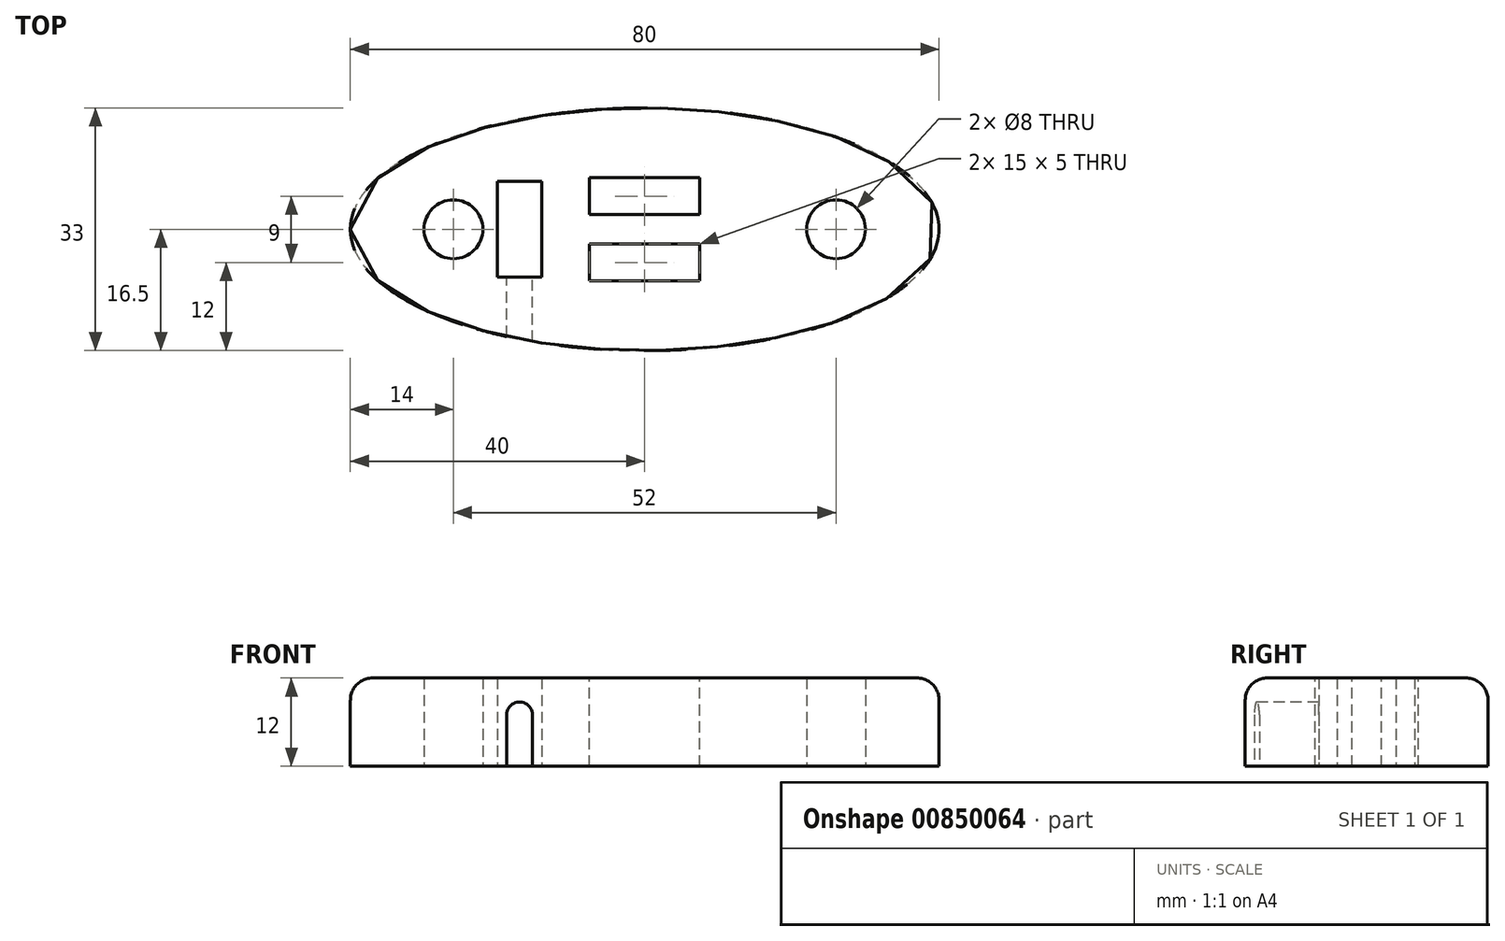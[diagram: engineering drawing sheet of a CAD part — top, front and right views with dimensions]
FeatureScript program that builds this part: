
annotation { "Feature Type Name" : "Feature", "Feature Type Description" : "" }
export const myFeature = defineFeature(function(context is Context, id is Id, definition is map)
    precondition{}
    {
        {
            var Q0;
            Q0=qCreatedBy(makeId("Top.planeOp"),FACE);
            var sketch = newSketch(context, id + "F0", { "sketchPlane" : qUnion([Q0])});
            skEllipse(sketch, "E0", {"center": v(0, 0) * mm, "majorRadius": 40 * mm, "minorRadius": 16.5 * mm, "majorAxis": v(-1, 0)});
            skSolve(sketch);
        }
        {
            var Q0;
            Q0 = qSketchRegion(id + "F0", true);
            extrude(context, id + "F1", {"entities" : qUnion([Q0]), "depth" : 12 * mm, "offsetDistance" : 25 * mm});
        }
        {
            var Q0;
            Q0=makeQuery(id+"F1.opExtrude","CAP_EDGE",EDGE,{"disambiguationData":[OSD([sQuery(id+"F0.wireOp",EDGE,"E0")])],"isStart":false});
            fillet(context, id + "F2", {"entities" : qUnion([Q0]), "radius" : 3 * mm, "tangentPropagation" : true, "allowEdgeOverflow" : false});
        }
        {
            var Q0;
            Q0=makeQuery(id+"F1.opExtrude","CAP_FACE",FACE,{"disambiguationData":[OSD([sQuery(id+"F0.wireOp",EDGE,"E0")])],"isStart":false});
            var sketch = newSketch(context, id + "F3", { "sketchPlane" : qUnion([Q0])});
            skLineSegment(sketch, "E1", {"start": v(0, 0) * mm, "end": v(0, -2) * mm});
            skLineSegment(sketch, "E2", {"start": v(0, -2) * mm, "end": v(-7.5, -2) * mm});
            skLineSegment(sketch, "E3.bottom", {"start": v(-7.5, -2) * mm, "end": v(7.5, -2) * mm});
            skLineSegment(sketch, "E3.top", {"start": v(-7.5, -7) * mm, "end": v(7.5, -7) * mm});
            skLineSegment(sketch, "E3.left", {"start": v(-7.5, -2) * mm, "end": v(-7.5, -7) * mm});
            skLineSegment(sketch, "E3.right", {"start": v(7.5, -2) * mm, "end": v(7.5, -7) * mm});
            skLineSegment(sketch, "E4", {"start": v(0, 0) * mm, "end": v(0, 2) * mm});
            skPoint(sketch, "E5.oppositeSnap0", {"position": v(7.5, -4.5) * mm});
            skLineSegment(sketch, "E5.bottom", {"start": v(-7.5, 2) * mm, "end": v(7.5, 2) * mm});
            skLineSegment(sketch, "E5.top", {"start": v(-7.5, 7) * mm, "end": v(7.5, 7) * mm});
            skLineSegment(sketch, "E5.left", {"start": v(-7.5, 2) * mm, "end": v(-7.5, 7) * mm});
            skLineSegment(sketch, "E5.right", {"start": v(7.5, 2) * mm, "end": v(7.5, 7) * mm});
            skSolve(sketch);
        }
        {
            var Q0;
            Q0=makeQuery(id+"F3.imprint","IMPRINT",FACE,{"disambiguationData":[TD([[makeQuery(id+"F3.imprint","IMPRINT",EDGE,{"derivedFrom":sQuery(id+"F3.wireOp",EDGE,"E3.top")}),1.0]])]});
            var Q1;
            Q1=makeQuery(id+"F3.imprint","IMPRINT",FACE,{"disambiguationData":[TD([[makeQuery(id+"F3.imprint","IMPRINT",EDGE,{"derivedFrom":sQuery(id+"F3.wireOp",EDGE,"E5.top")}),-1.0]])]});
            extrude(context, id + "F4", {"entities" : qUnion([Q0, Q1]), "operationType" : NewBodyOperationType.REMOVE, "endBound" : BoundingType.THROUGH_ALL, "oppositeDirection" : true, "depth" : 18.8 * mm, "offsetDistance" : 25 * mm});
        }
        {
            var Q0;
            Q0=makeQuery(id+"F1.opExtrude","CAP_FACE",FACE,{"disambiguationData":[OSD([sQuery(id+"F0.wireOp",EDGE,"E0")])],"isStart":true});
            var sketch = newSketch(context, id + "F5", { "sketchPlane" : qUnion([Q0])});
            skLineSegment(sketch, "E6", {"start": v(40, 0) * mm, "end": v(26, 0) * mm});
            skLineSegment(sketch, "E7", {"start": v(-40, 0) * mm, "end": v(-26, 0) * mm});
            skCircle(sketch, "E8", {"center": v(26, 0) * mm, "radius": 4 * mm});
            skCircle(sketch, "E9", {"center": v(-26, 0) * mm, "radius": 4 * mm});
            skLineSegment(sketch, "E10", {"start": v(-26, 0) * mm, "end": v(-20, 0) * mm});
            skLineSegment(sketch, "E11", {"start": v(-20, 0) * mm, "end": v(-20, -6.5) * mm});
            skLineSegment(sketch, "E12.bottom", {"start": v(-20, -6.5) * mm, "end": v(-14, -6.5) * mm});
            skLineSegment(sketch, "E12.top", {"start": v(-20, 6.5) * mm, "end": v(-14, 6.5) * mm});
            skLineSegment(sketch, "E12.left", {"start": v(-20, -6.5) * mm, "end": v(-20, 6.5) * mm});
            skLineSegment(sketch, "E12.right", {"start": v(-14, -6.5) * mm, "end": v(-14, 6.5) * mm});
            skSolve(sketch);
        }
        {
            var Q0;
            Q0 = qSketchRegion(id + "F5", true);
            extrude(context, id + "F6", {"entities" : qUnion([Q0]), "operationType" : NewBodyOperationType.REMOVE, "oppositeDirection" : true, "depth" : 53.1 * mm, "offsetDistance" : 25 * mm});
        }
        {
            var Q0;
            Q0=makeQuery(id+"F6.boolean.opBoolean","COPY",FACE,{"derivedFrom":makeQuery(id+"F6.opExtrude","SWEPT_FACE",FACE,{"disambiguationData":[OSD([sQuery(id+"F5.wireOp",EDGE,"E12.top")])]})});
            var sketch = newSketch(context, id + "F7", { "sketchPlane" : qUnion([Q0])});
            skLineSegment(sketch, "E13", {"start": v(17, 0) * mm, "end": v(17, 7) * mm});
            skLineSegment(sketch, "E14", {"start": v(17, 0) * mm, "end": v(15, 0) * mm});
            skCircle(sketch, "E15", {"center": v(17, 7) * mm, "radius": 1.75 * mm});
            skLineSegment(sketch, "E16", {"start": v(15.25, 7) * mm, "end": v(15.25, 0) * mm});
            skLineSegment(sketch, "E17", {"start": v(18.75, 7) * mm, "end": v(18.75, 0) * mm});
            skSolve(sketch);
        }
        {
            var Q0;
            {var subQ0=sQuery(id+"F7.wireOp",EDGE,"qlNYMipe-BtAs-6Y4S-IRvH-gPQyJQVTGbDt");var subQ1=sQuery(id+"F7.wireOp",EDGE,"E13");var subQ2=makeQuery(id+"F7.imprint","INTERSECT",VERTEX,{"derivedFrom":[subQ1,subQ0]});Q0=makeQuery(id+"F7.imprint","IMPRINT",FACE,{"disambiguationData":[TD([[makeQuery(id+"F7.imprint","IMPRINT",EDGE,{"disambiguationData":[TD([[subQ2,1.0]])],"derivedFrom":subQ1}),-1.0]])]});}
            var Q1;
            {var subQ0=sQuery(id+"F7.wireOp",EDGE,"qlNYMipe-BtAs-6Y4S-IRvH-gPQyJQVTGbDt");var subQ1=sQuery(id+"F7.wireOp",EDGE,"E13");var subQ2=makeQuery(id+"F7.imprint","INTERSECT",VERTEX,{"derivedFrom":[subQ1,subQ0]});Q1=makeQuery(id+"F7.imprint","IMPRINT",FACE,{"disambiguationData":[TD([[makeQuery(id+"F7.imprint","IMPRINT",EDGE,{"disambiguationData":[TD([[subQ2,1.0]])],"derivedFrom":subQ1}),1.0]])]});}
            var Q2;
            {var subQ0=sQuery(id+"F7.wireOp",EDGE,"qlNYMipe-BtAs-6Y4S-IRvH-gPQyJQVTGbDt");var subQ4=makeQuery(id+"F7.imprint","INTERSECT",VERTEX,{"derivedFrom":[sQuery(id+"F7.wireOp",EDGE,"E13"),subQ0]});Q2=makeQuery(id+"F7.imprint","IMPRINT",FACE,{"disambiguationData":[TD([[makeQuery(id+"F7.imprint","IMPRINT",EDGE,{"disambiguationData":[TD([[subQ4,1.0]])],"derivedFrom":subQ0}),1.0]])]});}
            var Q3;
            {var subQ0=sQuery(id+"F7.wireOp",EDGE,"E14");Q3=makeQuery(id+"F7.imprint","IMPRINT",FACE,{"disambiguationData":[TD([[makeQuery(id+"F7.imprint","IMPRINT",EDGE,{"derivedFrom":subQ0}),-1.0]])]});}
            var Q4;
            {var subQ5=sQuery(id+"F7.wireOp",EDGE,"R0LXtj1R-5Qjl-jMfm-QYCO-B6j8cCBFjxp5");Q4=makeQuery(id+"F7.imprint","IMPRINT",FACE,{"disambiguationData":[TD([[makeQuery(id+"F7.imprint","IMPRINT",EDGE,{"derivedFrom":subQ5}),-1.0]])]});}
            var Q5;
            {var subQ0=sQuery(id+"F7.wireOp",EDGE,"E15");var subQ1=makeQuery(id+"F7.imprint","INTERSECT",VERTEX,{"derivedFrom":[subQ0,sQuery(id+"F7.wireOp",EDGE,"E16")]});Q5=makeQuery(id+"F7.imprint","IMPRINT",FACE,{"disambiguationData":[TD([[makeQuery(id+"F7.imprint","IMPRINT",EDGE,{"disambiguationData":[TD([[subQ1,1.0]])],"derivedFrom":subQ0}),1.0]])]});}
            extrude(context, id + "F8", {"entities" : qUnion([Q0, Q1, Q2, Q3, Q4, Q5]), "operationType" : NewBodyOperationType.REMOVE, "oppositeDirection" : true, "depth" : 25 * mm, "offsetDistance" : 25 * mm});
        }
    });
